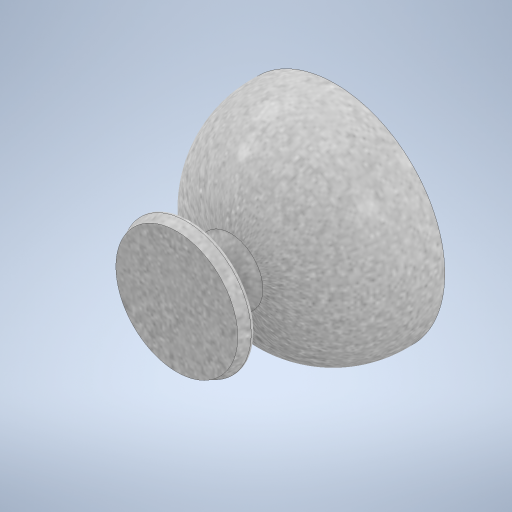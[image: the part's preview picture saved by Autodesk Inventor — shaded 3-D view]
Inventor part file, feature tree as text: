
AUTODESK INVENTOR PART (.ipt)
format: ipt  version: 2024 (Build 280153000, 153)  size: 383,488 bytes
history: native  units: mm
features: revolve x1, fillet x1, shell x1, sketch x1
ambient origin geometry x8: Origin, YZ Plane, XZ Plane, XY Plane, X Axis, Y Axis, Z Axis, Center Point
bodies: Volumenkörper1 (feature_tree)
feature tree (4):
  revolve  "Umdrehung1"
  fillet  "Rundung2"  Radius=65.0mm
  shell  "Wandung2"  Thickness=30.0mm
  sketch  "Skizze1"  dims[d4=50.0mm d5=90.0mm d6=7.0mm d7=3.778638mm d8=42.0mm d9=5.0mm d10=360.0deg d13=1.0mm d15=4.0mm d16=0.0mm d17=0.0mm d18=0.0mm d19=0.0mm]
